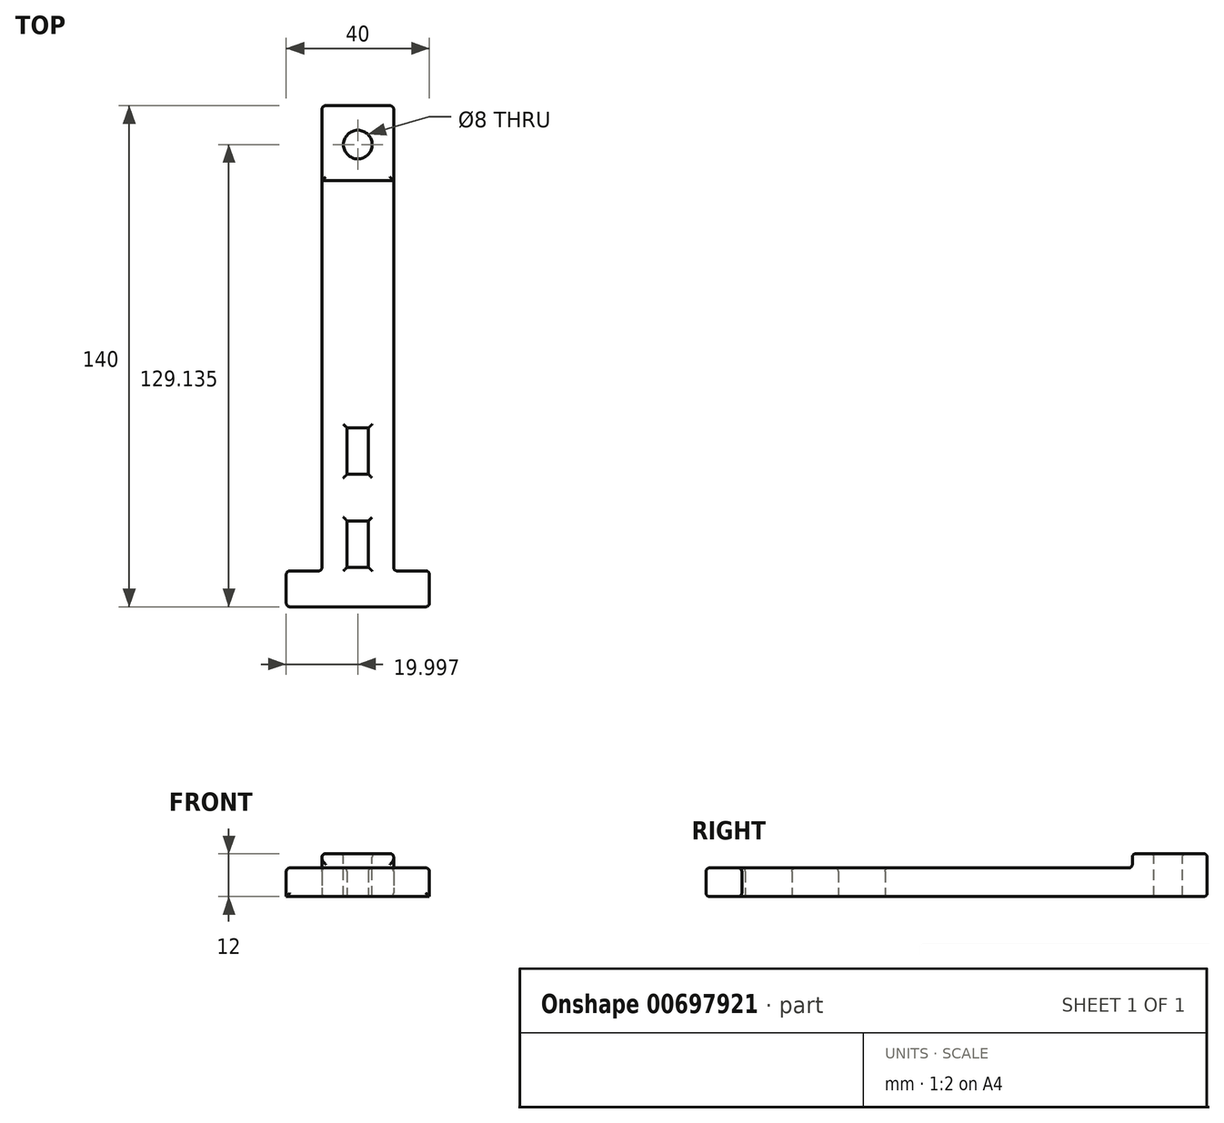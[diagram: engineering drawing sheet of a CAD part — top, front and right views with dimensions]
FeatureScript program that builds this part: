
annotation { "Feature Type Name" : "Feature", "Feature Type Description" : "" }
export const myFeature = defineFeature(function(context is Context, id is Id, definition is map)
    precondition{}
    {
        {
            var Q0;
            Q0=qCreatedBy(makeId("Top.planeOp"),FACE);
            var sketch = newSketch(context, id + "F0", { "sketchPlane" : qUnion([Q0])});
            skLineSegment(sketch, "E0.bottom", {"start": v(-56.55, 130.63) * mm, "end": v(-36.55, 130.63) * mm});
            skLineSegment(sketch, "E0.top", {"start": v(-56.55, -9.37) * mm, "end": v(-36.55, -9.37) * mm});
            skLineSegment(sketch, "E0.left", {"start": v(-56.55, 130.63) * mm, "end": v(-56.55, -9.37) * mm});
            skLineSegment(sketch, "E0.right", {"start": v(-36.55, 130.63) * mm, "end": v(-36.55, -9.37) * mm});
            skLineSegment(sketch, "E1.bottom", {"start": v(-49.55, 40.63) * mm, "end": v(-43.55, 40.63) * mm});
            skLineSegment(sketch, "E1.top", {"start": v(-49.55, 27.63) * mm, "end": v(-43.55, 27.63) * mm});
            skLineSegment(sketch, "E1.left", {"start": v(-49.55, 40.63) * mm, "end": v(-49.55, 27.63) * mm});
            skLineSegment(sketch, "E1.right", {"start": v(-43.55, 40.63) * mm, "end": v(-43.55, 27.63) * mm});
            skLineSegment(sketch, "E2.bottom", {"start": v(-49.55, 14.63) * mm, "end": v(-43.55, 14.63) * mm});
            skLineSegment(sketch, "E2.top", {"start": v(-49.55, 1.63) * mm, "end": v(-43.55, 1.63) * mm});
            skLineSegment(sketch, "E2.left", {"start": v(-49.55, 14.63) * mm, "end": v(-49.55, 1.63) * mm});
            skLineSegment(sketch, "E2.right", {"start": v(-43.55, 14.63) * mm, "end": v(-43.55, 1.63) * mm});
            skLineSegment(sketch, "E3", {"start": v(-46.55, 130.63) * mm, "end": v(-46.55, -9.37) * mm, "construction": true});
            skLineSegment(sketch, "E4.bottom", {"start": v(-66.55, -9.37) * mm, "end": v(-26.55, -9.37) * mm});
            skLineSegment(sketch, "E4.top", {"start": v(-66.55, 0.63) * mm, "end": v(-26.55, 0.63) * mm});
            skLineSegment(sketch, "E4.left", {"start": v(-66.55, -9.37) * mm, "end": v(-66.55, 0.63) * mm});
            skLineSegment(sketch, "E4.right", {"start": v(-26.55, -9.37) * mm, "end": v(-26.55, 0.63) * mm});
            skSolve(sketch);
        }
        {
            var Q0;
            Q0 = qSketchRegion(id + "F0", true);
            extrude(context, id + "F1", {"entities" : qUnion([Q0]), "depth" : 8 * mm, "offsetDistance" : 25 * mm});
        }
        {
            var Q0;
            Q0=makeQuery(id+"F1.opExtrude","CAP_FACE",FACE,{"disambiguationData":[OSD([sQuery(id+"F0.wireOp",EDGE,"E0.bottom"),sQuery(id+"F0.wireOp",EDGE,"E0.left"),sQuery(id+"F0.wireOp",EDGE,"E0.right"),sQuery(id+"F0.wireOp",EDGE,"E1.bottom"),sQuery(id+"F0.wireOp",EDGE,"E1.top"),sQuery(id+"F0.wireOp",EDGE,"E1.left"),sQuery(id+"F0.wireOp",EDGE,"E1.right"),sQuery(id+"F0.wireOp",EDGE,"E2.bottom"),sQuery(id+"F0.wireOp",EDGE,"E2.top"),sQuery(id+"F0.wireOp",EDGE,"E2.left"),sQuery(id+"F0.wireOp",EDGE,"E2.right"),sQuery(id+"F0.wireOp",EDGE,"PTGagxfs-ajq4-6Odk-Gujg-U9b2UgT4rP4k"),sQuery(id+"F0.wireOp",EDGE,"O5Vd3rXp-Kzfb-9a31-HQef-GEPcJxw7OYIo"),sQuery(id+"F0.wireOp",EDGE,"GYkmYROb-XP6c-3AC7-PmiQ-gQp7UfHpjOtQ")])],"isStart":false});
            var sketch = newSketch(context, id + "F2", { "sketchPlane" : qUnion([Q0])});
            skLineSegment(sketch, "E5.bottom", {"start": v(-56.55, 130.63) * mm, "end": v(-36.55, 130.63) * mm});
            skLineSegment(sketch, "E5.top", {"start": v(-56.55, 109.72) * mm, "end": v(-36.55, 109.72) * mm});
            skLineSegment(sketch, "E5.left", {"start": v(-56.55, 130.63) * mm, "end": v(-56.55, 109.72) * mm});
            skLineSegment(sketch, "E5.right", {"start": v(-36.55, 130.63) * mm, "end": v(-36.55, 109.72) * mm});
            skCircle(sketch, "E6", {"center": v(-46.55, 119.77) * mm, "radius": 4 * mm});
            skPoint(sketch, "E6.centerSnap0", {"position": v(-46.55, 130.63) * mm});
            skSolve(sketch);
        }
        {
            var Q0;
            Q0=makeQuery(id+"F2.imprint","IMPRINT",FACE,{"disambiguationData":[TD([[makeQuery(id+"F2.imprint","IMPRINT",EDGE,{"derivedFrom":sQuery(id+"F2.wireOp",EDGE,"E6")}),1.0]])]});
            extrude(context, id + "F3", {"entities" : qUnion([Q0]), "operationType" : NewBodyOperationType.REMOVE, "endBound" : BoundingType.SYMMETRIC, "oppositeDirection" : true, "depth" : 100 * mm, "offsetDistance" : 25 * mm});
        }
        {
            var Q0;
            Q0=makeQuery(id+"F2.imprint","IMPRINT",FACE,{"disambiguationData":[TD([[makeQuery(id+"F2.imprint","IMPRINT",EDGE,{"derivedFrom":sQuery(id+"F2.wireOp",EDGE,"E5.bottom")}),-1.0]])]});
            extrude(context, id + "F4", {"entities" : qUnion([Q0]), "operationType" : NewBodyOperationType.ADD, "depth" : 4 * mm, "offsetDistance" : 25 * mm});
        }
        {
            var Q0;
            Q0=makeQuery(id+"F1.opExtrude","CAP_FACE",FACE,{"disambiguationData":[OSD([sQuery(id+"F0.wireOp",EDGE,"E0.bottom"),sQuery(id+"F0.wireOp",EDGE,"E0.left"),sQuery(id+"F0.wireOp",EDGE,"E0.right"),sQuery(id+"F0.wireOp",EDGE,"E1.bottom"),sQuery(id+"F0.wireOp",EDGE,"E1.top"),sQuery(id+"F0.wireOp",EDGE,"E1.left"),sQuery(id+"F0.wireOp",EDGE,"E1.right"),sQuery(id+"F0.wireOp",EDGE,"E2.bottom"),sQuery(id+"F0.wireOp",EDGE,"E2.top"),sQuery(id+"F0.wireOp",EDGE,"E2.left"),sQuery(id+"F0.wireOp",EDGE,"E2.right"),sQuery(id+"F0.wireOp",EDGE,"E4.bottom"),sQuery(id+"F0.wireOp",EDGE,"E4.top"),sQuery(id+"F0.wireOp",EDGE,"E4.left"),sQuery(id+"F0.wireOp",EDGE,"E4.right")])],"isStart":false});
            var Q1;
            Q1=makeQuery(id+"F1.opExtrude","CAP_EDGE",EDGE,{"disambiguationData":[OSD([sQuery(id+"F0.wireOp",EDGE,"E0.right")])],"isStart":true});
            var Q2;
            Q2=makeQuery(id+"F1.opExtrude","CAP_EDGE",EDGE,{"disambiguationData":[OSD([sQuery(id+"F0.wireOp",EDGE,"E0.left")])],"isStart":true});
            var Q3;
            Q3=makeQuery(id+"F4.opExtrude","CAP_FACE",FACE,{"disambiguationData":[OSD([sQuery(id+"F2.wireOp",EDGE,"E5.bottom"),sQuery(id+"F2.wireOp",EDGE,"E5.top"),sQuery(id+"F2.wireOp",EDGE,"E5.left"),sQuery(id+"F2.wireOp",EDGE,"E5.right"),sQuery(id+"F2.wireOp",EDGE,"E6")])],"isStart":false});
            var Q4;
            {var subQ0=sQuery(id+"F0.wireOp",EDGE,"E4.top");Q4=makeQuery(id+"F1.opExtrude","SWEPT_FACE",FACE,{"disambiguationData":[OSD([subQ0]),TDD([makeQuery(id+"F0.imprint","IMPRINT",EDGE,{"disambiguationData":[TD([[makeQuery(id+"F0.imprint","INTERSECT",VERTEX,{"derivedFrom":[subQ0,sQuery(id+"F0.wireOp",EDGE,"E4.right")]}),1.0]])],"derivedFrom":subQ0})])]});}
            var Q5;
            {var subQ0=sQuery(id+"F0.wireOp",EDGE,"E4.top");Q5=makeQuery(id+"F1.opExtrude","SWEPT_FACE",FACE,{"disambiguationData":[OSD([subQ0]),TDD([makeQuery(id+"F0.imprint","IMPRINT",EDGE,{"disambiguationData":[TD([[makeQuery(id+"F0.imprint","INTERSECT",VERTEX,{"derivedFrom":[subQ0,sQuery(id+"F0.wireOp",EDGE,"E4.left")]}),-1.0]])],"derivedFrom":subQ0})])]});}
            var Q6;
            Q6=makeQuery(id+"F4.boolean.opBoolean","MERGE",FACE,{"derivedFrom":[makeQuery(id+"F1.opExtrude","SWEPT_FACE",FACE,{"disambiguationData":[OSD([sQuery(id+"F0.wireOp",EDGE,"E0.bottom")])]}),makeQuery(id+"F4.opExtrude","SWEPT_FACE",FACE,{"disambiguationData":[OSD([sQuery(id+"F2.wireOp",EDGE,"E5.bottom")])]})]});
            var Q7;
            Q7=makeQuery(id+"F1.opExtrude","SWEPT_FACE",FACE,{"disambiguationData":[OSD([sQuery(id+"F0.wireOp",EDGE,"E4.bottom")])]});
            fillet(context, id + "F5", {"entities" : qUnion([Q0, Q1, Q2, Q3, Q4, Q5, Q6, Q7]), "radius" : 1 * mm, "tangentPropagation" : true, "allowEdgeOverflow" : false});
        }
    });
